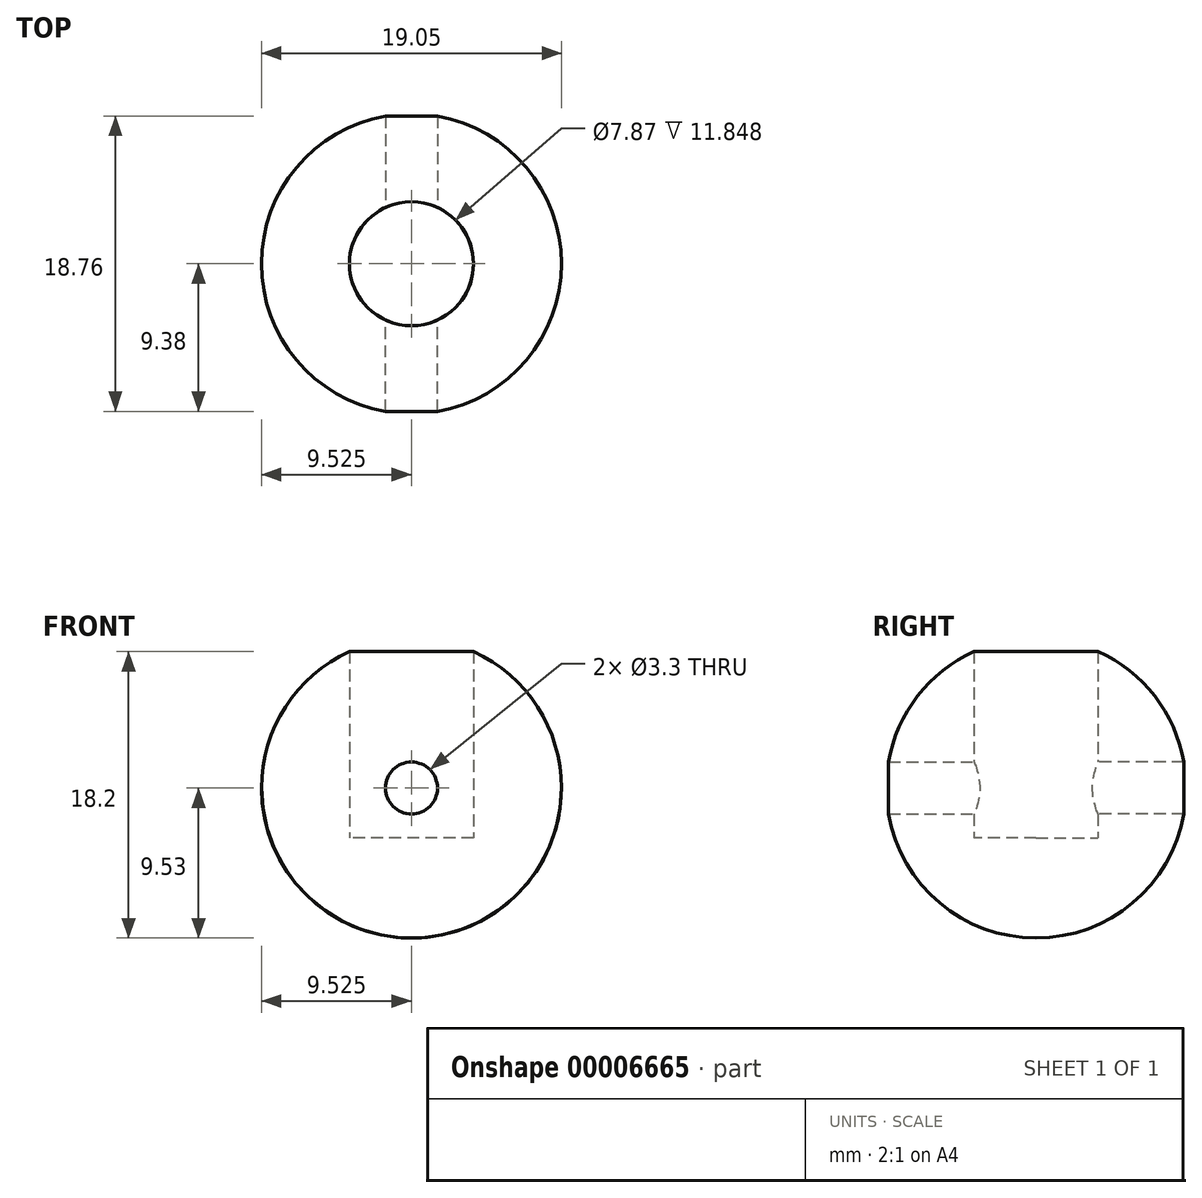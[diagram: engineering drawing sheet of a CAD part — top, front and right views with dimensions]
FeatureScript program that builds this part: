
annotation { "Feature Type Name" : "Feature", "Feature Type Description" : "" }
export const myFeature = defineFeature(function(context is Context, id is Id, definition is map)
    precondition{}
    {
        {
            var Q0;
            Q0=qCreatedBy(makeId("Front.planeOp"),FACE);
            var sketch = newSketch(context, id + "F0", { "sketchPlane" : qUnion([Q0])});
            skLineSegment(sketch, "E0", {"start": v(0, 0) * mm, "end": v(19.05, 0) * mm});
            skArc(sketch, "E1", {"start": v(0, 0) * mm, "mid": v(9.53, -9.53) * mm, "end": v(19.05, 0) * mm});
            skSolve(sketch);
        }
        {
            var Q0;
            Q0=makeQuery(id+"F0.imprint","IMPRINT",FACE,{"disambiguationData":[TD([[makeQuery(id+"F0.imprint","IMPRINT",EDGE,{"derivedFrom":sQuery(id+"F0.wireOp",EDGE,"E0")}),-1.0]])]});
            var Q1;
            Q1=sQuery(id+"F0.wireOp",EDGE,"E0");
            revolve(context, id + "F1", {"entities" : qUnion([Q0]), "axis" : qUnion([Q1]), "revolveType" : RevolveType.FULL});
        }
        {
            var Q0;
            Q0=qCreatedBy(makeId("Top.planeOp"),FACE);
            var sketch = newSketch(context, id + "F2", { "sketchPlane" : qUnion([Q0])});
            skLineSegment(sketch, "E2", {"start": v(0, 0) * mm, "end": v(9.53, 0) * mm});
            skCircle(sketch, "E3", {"center": v(9.53, 0) * mm, "radius": 3.94 * mm});
            skSolve(sketch);
        }
        {
            var Q0;
            Q0 = qSketchRegion(id + "F2", true);
            extrude(context, id + "F3", {"entities" : qUnion([Q0]), "operationType" : NewBodyOperationType.REMOVE, "depth" : 25.4 * mm});
        }
        {
            var Q0;
            Q0 = qSketchRegion(id + "F2", true);
            extrude(context, id + "F4", {"entities" : qUnion([Q0]), "operationType" : NewBodyOperationType.REMOVE, "oppositeDirection" : true, "depth" : 3.17 * mm});
        }
        {
            var Q0;
            Q0=qCreatedBy(makeId("Front.planeOp"),FACE);
            var sketch = newSketch(context, id + "F5", { "sketchPlane" : qUnion([Q0])});
            skLineSegment(sketch, "E4", {"start": v(0, 0) * mm, "end": v(9.52, 0) * mm});
            skCircle(sketch, "E5", {"center": v(9.52, 0) * mm, "radius": 1.65 * mm});
            skSolve(sketch);
        }
        {
            var Q0;
            Q0 = qSketchRegion(id + "F5", true);
            extrude(context, id + "F6", {"entities" : qUnion([Q0]), "operationType" : NewBodyOperationType.REMOVE, "oppositeDirection" : true, "depth" : 25.4 * mm});
        }
        {
            var Q0;
            Q0 = qSketchRegion(id + "F5", true);
            extrude(context, id + "F7", {"entities" : qUnion([Q0]), "operationType" : NewBodyOperationType.REMOVE, "depth" : 25.4 * mm});
        }
    });
